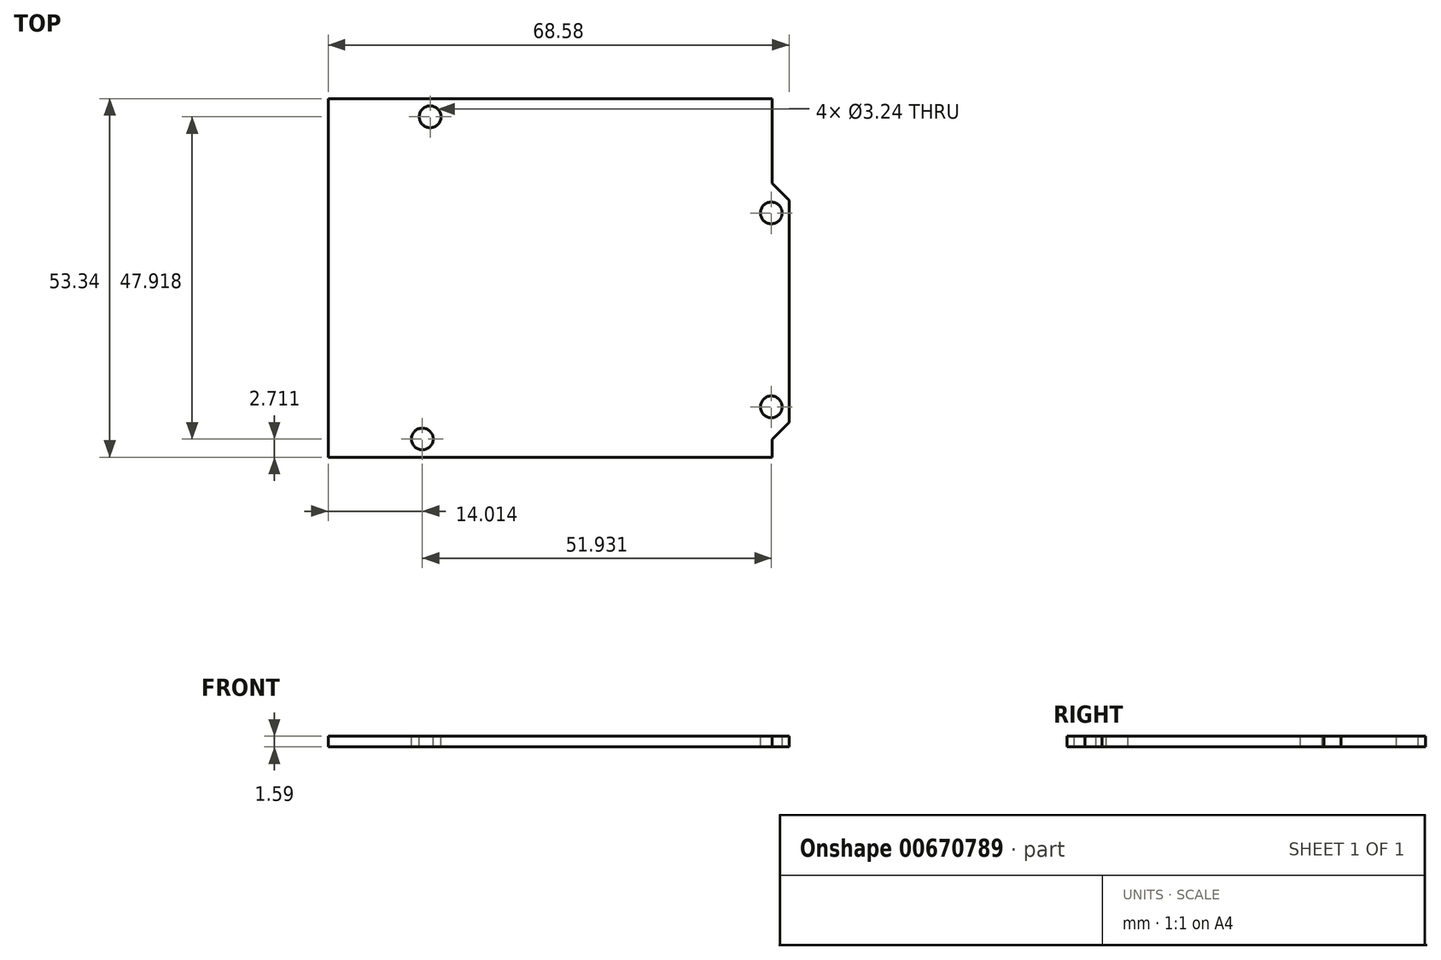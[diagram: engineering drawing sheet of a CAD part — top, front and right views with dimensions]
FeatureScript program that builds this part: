
annotation { "Feature Type Name" : "Feature", "Feature Type Description" : "" }
export const myFeature = defineFeature(function(context is Context, id is Id, definition is map)
    precondition{}
    {
        {
            var Q0;
            Q0=qCreatedBy(makeId("Top.planeOp"),FACE);
            var sketch = newSketch(context, id + "F0", { "sketchPlane" : qUnion([Q0])});
            skLineSegment(sketch, "E0", {"start": v(-33.02, 26.67) * mm, "end": v(33.02, 26.67) * mm});
            skLineSegment(sketch, "E1", {"start": v(33.02, -26.67) * mm, "end": v(-33.02, -26.67) * mm});
            skLineSegment(sketch, "E2", {"start": v(-33.02, 26.67) * mm, "end": v(-33.02, -26.67) * mm});
            skLineSegment(sketch, "E3", {"start": v(33.02, 26.67) * mm, "end": v(33.02, 14.1) * mm});
            skLineSegment(sketch, "E4", {"start": v(0, 0) * mm, "end": v(0, 26.67) * mm, "construction": true});
            skLineSegment(sketch, "E5", {"start": v(0, 0) * mm, "end": v(-33.02, 0) * mm, "construction": true});
            skLineSegment(sketch, "E6", {"start": v(35.56, -21.46) * mm, "end": v(35.56, 11.56) * mm});
            skLineSegment(sketch, "E7", {"start": v(35.56, 11.56) * mm, "end": v(33.02, 14.1) * mm});
            skLineSegment(sketch, "E8", {"start": v(35.56, -21.46) * mm, "end": v(33.02, -24) * mm});
            skLineSegment(sketch, "E9.trimOffspring", {"start": v(33.02, -24) * mm, "end": v(33.02, -26.67) * mm});
            skSolve(sketch);
        }
        {
            var Q0;
            Q0 = qSketchRegion(id + "F0", true);
            extrude(context, id + "F1", {"entities" : qUnion([Q0]), "depth" : 1.59 * mm, "offsetDistance" : 25 * mm});
        }
        {
            var Q0;
            Q0=makeQuery(id+"F1.opExtrude","CAP_FACE",FACE,{"disambiguationData":[OSD([sQuery(id+"F0.wireOp",EDGE,"E0"),sQuery(id+"F0.wireOp",EDGE,"E1"),sQuery(id+"F0.wireOp",EDGE,"E2"),sQuery(id+"F0.wireOp",EDGE,"E3"),sQuery(id+"F0.wireOp",EDGE,"E6"),sQuery(id+"F0.wireOp",EDGE,"E7"),sQuery(id+"F0.wireOp",EDGE,"E8"),sQuery(id+"F0.wireOp",EDGE,"E9.trimOffspring")])],"isStart":false});
            var sketch = newSketch(context, id + "F2", { "sketchPlane" : qUnion([Q0])});
            skCircle(sketch, "E10", {"center": v(-19, -23.96) * mm, "radius": 1.62 * mm});
            skCircle(sketch, "E11", {"center": v(-17.84, 23.96) * mm, "radius": 1.62 * mm});
            skCircle(sketch, "E12", {"center": v(32.93, -19.19) * mm, "radius": 1.62 * mm});
            skCircle(sketch, "E13", {"center": v(32.93, 9.66) * mm, "radius": 1.62 * mm});
            skSolve(sketch);
        }
        {
            var Q0;
            Q0 = qSketchRegion(id + "F2", true);
            extrude(context, id + "F3", {"entities" : qUnion([Q0]), "operationType" : NewBodyOperationType.REMOVE, "oppositeDirection" : true, "depth" : 25 * mm, "offsetDistance" : 25 * mm});
        }
    });
